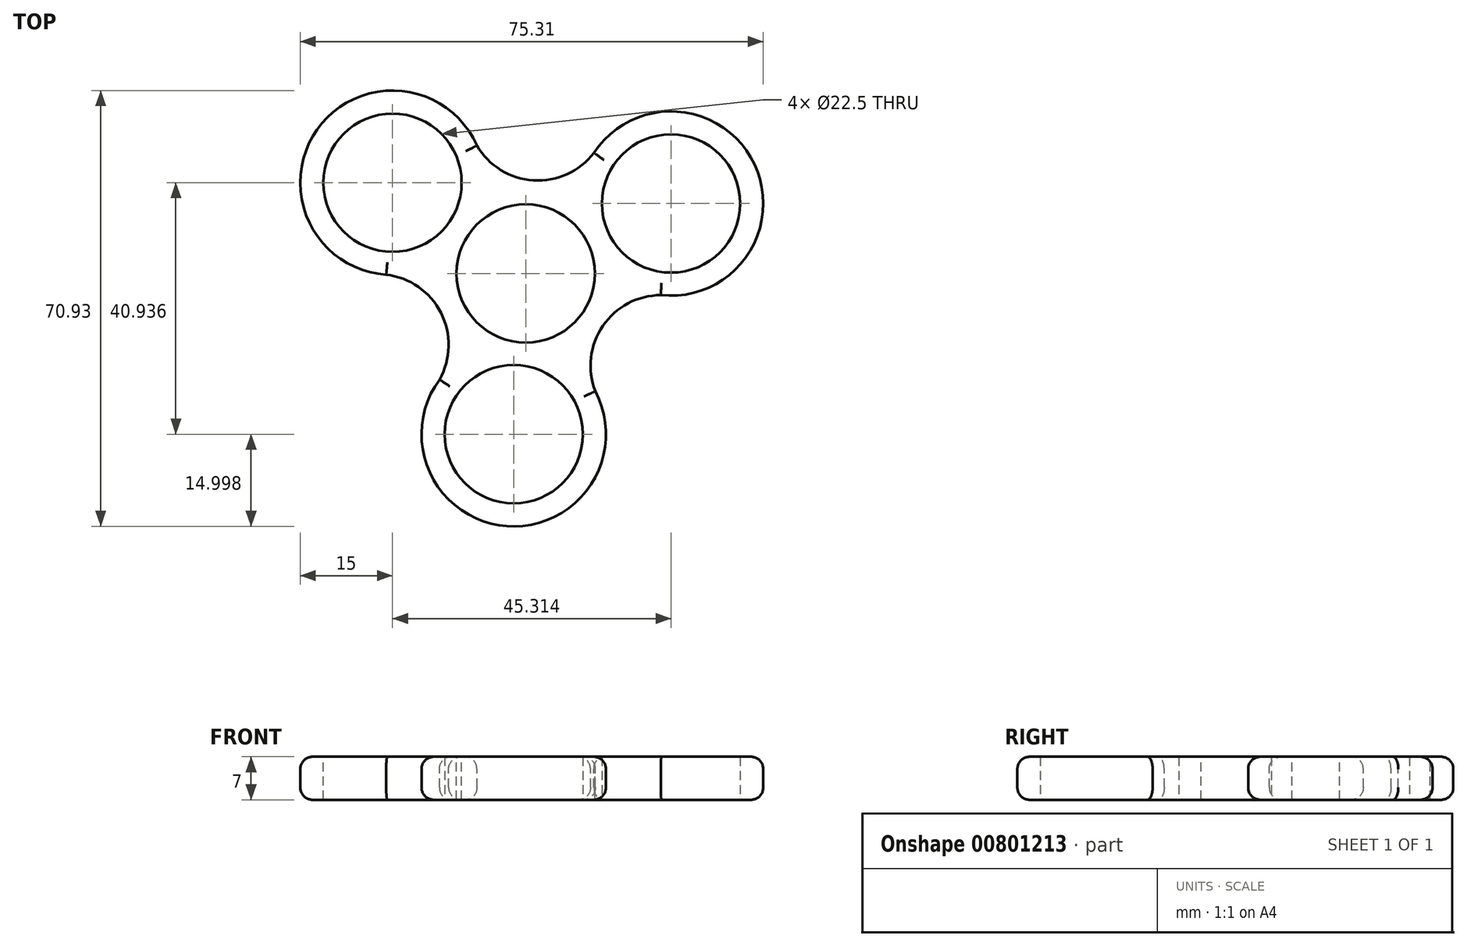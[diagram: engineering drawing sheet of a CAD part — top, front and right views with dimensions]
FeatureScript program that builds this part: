
annotation { "Feature Type Name" : "Feature", "Feature Type Description" : "" }
export const myFeature = defineFeature(function(context is Context, id is Id, definition is map)
    precondition{}
    {
        {
            var Q0;
            Q0=qCreatedBy(makeId("Top.planeOp"),FACE);
            var sketch = newSketch(context, id + "F0", { "sketchPlane" : qUnion([Q0])});
            skCircle(sketch, "E0", {"center": v(0, 0) * mm, "radius": 15 * mm});
            skSolve(sketch);
        }
        {
            var Q0;
            Q0=makeQuery(id+"F0.imprint","IMPRINT",FACE,{"disambiguationData":[TD([[makeQuery(id+"F0.imprint","IMPRINT",EDGE,{"derivedFrom":sQuery(id+"F0.wireOp",EDGE,"E0")}),1.0]])]});
            extrude(context, id + "F1", {"entities" : qUnion([Q0]), "depth" : 7 * mm, "offsetDistance" : 25 * mm});
        }
        {
            var Q0;
            Q0=makeQuery(id+"F1.opExtrude","CAP_EDGE",EDGE,{"disambiguationData":[OSD([sQuery(id+"F0.wireOp",EDGE,"E0")])],"isStart":true});
            fillet(context, id + "F2", {"entities" : qUnion([Q0]), "radius" : 2 * mm, "tangentPropagation" : true, "allowEdgeOverflow" : false});
        }
        {
            var Q0;
            Q0=makeQuery(id+"F1.opExtrude","CAP_EDGE",EDGE,{"disambiguationData":[OSD([sQuery(id+"F0.wireOp",EDGE,"E0")])],"isStart":false});
            fillet(context, id + "F3", {"entities" : qUnion([Q0]), "radius" : 2 * mm, "tangentPropagation" : true, "allowEdgeOverflow" : false});
        }
        {
            var Q0;
            Q0=makeQuery(id+"F1.opExtrude","CAP_FACE",FACE,{"disambiguationData":[OSD([sQuery(id+"F0.wireOp",EDGE,"E0")])],"isStart":false});
            var sketch = newSketch(context, id + "F4", { "sketchPlane" : qUnion([Q0])});
            skCircle(sketch, "E1", {"center": v(0, 0) * mm, "radius": 11.25 * mm});
            skSolve(sketch);
        }
        {
            var Q0;
            Q0 = qSketchRegion(id + "F4", true);
            extrude(context, id + "F5", {"entities" : qUnion([Q0]), "operationType" : NewBodyOperationType.REMOVE, "oppositeDirection" : true, "depth" : 7 * mm, "offsetDistance" : 25 * mm});
        }
        {
            var Q0;
            Q0=makeQuery(id+"F1.opExtrude","CAP_FACE",FACE,{"disambiguationData":[OSD([sQuery(id+"F0.wireOp",EDGE,"E0")])],"isStart":true});
            var sketch = newSketch(context, id + "F6", { "sketchPlane" : qUnion([Q0])});
            skArc(sketch, "E2", {"start": v(3.97, 12.38) * mm, "mid": v(-3.07, 41.12) * mm, "end": v(-5.76, 11.65) * mm});
            skArc(sketch, "E3", {"start": v(3.97, 12.38) * mm, "mid": v(-0.97, 12.96) * mm, "end": v(-5.76, 11.65) * mm});
            skSolve(sketch);
        }
        {
            var Q0;
            {var subQ0=sQuery(id+"F6.wireOp",EDGE,"E2");Q0=makeQuery(id+"F6.imprint","IMPRINT",FACE,{"disambiguationData":[TD([[makeQuery(id+"F6.imprint","IMPRINT",EDGE,{"derivedFrom":subQ0}),1.0]])]});}
            extrude(context, id + "F7", {"entities" : qUnion([Q0]), "operationType" : NewBodyOperationType.ADD, "oppositeDirection" : true, "depth" : 7 * mm, "offsetDistance" : 25 * mm});
        }
        {
            var Q0;
            {var subQ0=sQuery(id+"F0.wireOp",EDGE,"E0");Q0=makeQuery(id+"F7.boolean.opBoolean","MERGE",FACE,{"derivedFrom":[makeQuery(id+"F1.opExtrude","CAP_FACE",FACE,{"disambiguationData":[OSD([subQ0])],"isStart":true}),makeQuery(id+"F7.opExtrude","CAP_FACE",FACE,{"disambiguationData":[OSD([subQ0,sQuery(id+"F6.wireOp",EDGE,"E2")])],"isStart":true})]});}
            var sketch = newSketch(context, id + "F8", { "sketchPlane" : qUnion([Q0])});
            skCircle(sketch, "E4", {"center": v(-1.95, 26.16) * mm, "radius": 11.25 * mm});
            skSolve(sketch);
        }
        {
            var Q0;
            Q0=makeQuery(id+"F8.imprint","IMPRINT",FACE,{"disambiguationData":[TD([[makeQuery(id+"F8.imprint","IMPRINT",EDGE,{"derivedFrom":sQuery(id+"F8.wireOp",EDGE,"E4")}),1.0]])]});
            extrude(context, id + "F9", {"entities" : qUnion([Q0]), "operationType" : NewBodyOperationType.REMOVE, "oppositeDirection" : true, "depth" : 7 * mm, "offsetDistance" : 25 * mm});
        }
        {
            var Q0;
            {var subQ0=sQuery(id+"F0.wireOp",EDGE,"E0");Q0=makeQuery(id+"F7.boolean.opBoolean","MERGE",FACE,{"derivedFrom":[makeQuery(id+"F1.opExtrude","CAP_FACE",FACE,{"disambiguationData":[OSD([subQ0])],"isStart":true}),makeQuery(id+"F7.opExtrude","CAP_FACE",FACE,{"disambiguationData":[OSD([subQ0,sQuery(id+"F6.wireOp",EDGE,"E2")])],"isStart":true})]});}
            var sketch = newSketch(context, id + "F10", { "sketchPlane" : qUnion([Q0])});
            skArc(sketch, "E5", {"start": v(8.74, -9.62) * mm, "mid": v(37.15, -17.9) * mm, "end": v(12.97, -0.84) * mm});
            skArc(sketch, "E6", {"start": v(12.97, -0.84) * mm, "mid": v(10.74, 7.32) * mm, "end": v(3.97, 12.38) * mm});
            skArc(sketch, "E7", {"start": v(8.74, -9.62) * mm, "mid": v(11.71, -5.64) * mm, "end": v(12.97, -0.84) * mm});
            skSolve(sketch);
        }
        {
            var Q0;
            {var subQ0=sQuery(id+"F10.wireOp",EDGE,"E5");Q0=makeQuery(id+"F10.imprint","IMPRINT",FACE,{"disambiguationData":[TD([[makeQuery(id+"F10.imprint","IMPRINT",EDGE,{"derivedFrom":subQ0}),1.0]])]});}
            extrude(context, id + "F11", {"entities" : qUnion([Q0]), "operationType" : NewBodyOperationType.ADD, "oppositeDirection" : true, "depth" : 7 * mm, "offsetDistance" : 25 * mm});
        }
        {
            var Q0;
            {var subQ0=sQuery(id+"F0.wireOp",EDGE,"E0");Q0=makeQuery(id+"F11.boolean.opBoolean","MERGE",FACE,{"derivedFrom":[makeQuery(id+"F7.boolean.opBoolean","MERGE",FACE,{"derivedFrom":[makeQuery(id+"F1.opExtrude","CAP_FACE",FACE,{"disambiguationData":[OSD([subQ0])],"isStart":true}),makeQuery(id+"F7.opExtrude","CAP_FACE",FACE,{"disambiguationData":[OSD([subQ0,sQuery(id+"F6.wireOp",EDGE,"E2")])],"isStart":true})]}),makeQuery(id+"F11.opExtrude","CAP_FACE",FACE,{"disambiguationData":[OSD([subQ0,sQuery(id+"F10.wireOp",EDGE,"E5")])],"isStart":true})]});}
            var sketch = newSketch(context, id + "F12", { "sketchPlane" : qUnion([Q0])});
            skCircle(sketch, "E8", {"center": v(23.63, -11.39) * mm, "radius": 11.25 * mm});
            skSolve(sketch);
        }
        {
            var Q0;
            Q0=makeQuery(id+"F12.imprint","IMPRINT",FACE,{"disambiguationData":[TD([[makeQuery(id+"F12.imprint","IMPRINT",EDGE,{"derivedFrom":sQuery(id+"F12.wireOp",EDGE,"E8")}),1.0]])]});
            extrude(context, id + "F13", {"entities" : qUnion([Q0]), "operationType" : NewBodyOperationType.REMOVE, "oppositeDirection" : true, "depth" : 7 * mm, "offsetDistance" : 25 * mm});
        }
        {
            var Q0;
            {var subQ0=sQuery(id+"F0.wireOp",EDGE,"E0");Q0=makeQuery(id+"F11.boolean.opBoolean","MERGE",FACE,{"derivedFrom":[makeQuery(id+"F7.boolean.opBoolean","MERGE",FACE,{"derivedFrom":[makeQuery(id+"F1.opExtrude","CAP_FACE",FACE,{"disambiguationData":[OSD([subQ0])],"isStart":false}),makeQuery(id+"F7.opExtrude","CAP_FACE",FACE,{"disambiguationData":[OSD([subQ0,sQuery(id+"F6.wireOp",EDGE,"E2")])],"isStart":false})]}),makeQuery(id+"F11.opExtrude","CAP_FACE",FACE,{"disambiguationData":[OSD([subQ0,sQuery(id+"F10.wireOp",EDGE,"E5")])],"isStart":false})]});}
            var sketch = newSketch(context, id + "F14", { "sketchPlane" : qUnion([Q0])});
            skArc(sketch, "E9", {"start": v(-7.21, 10.82) * mm, "mid": v(-34.08, 23.22) * mm, "end": v(-12.7, 2.76) * mm});
            skArc(sketch, "E10", {"start": v(8.74, 9.62) * mm, "mid": v(0.97, 12.96) * mm, "end": v(-7.21, 10.82) * mm});
            skArc(sketch, "E11", {"start": v(-12.7, 2.76) * mm, "mid": v(-11.71, -5.64) * mm, "end": v(-5.76, -11.65) * mm});
            skArc(sketch, "E12", {"start": v(-7.21, 10.82) * mm, "mid": v(-10.74, 7.32) * mm, "end": v(-12.7, 2.76) * mm});
            skSolve(sketch);
        }
        {
            var Q0;
            {var subQ0=sQuery(id+"F14.wireOp",EDGE,"E9");Q0=makeQuery(id+"F14.imprint","IMPRINT",FACE,{"disambiguationData":[TD([[makeQuery(id+"F14.imprint","IMPRINT",EDGE,{"derivedFrom":subQ0}),1.0]])]});}
            extrude(context, id + "F15", {"entities" : qUnion([Q0]), "operationType" : NewBodyOperationType.ADD, "oppositeDirection" : true, "depth" : 7 * mm, "offsetDistance" : 25 * mm});
        }
        {
            var Q0;
            {var subQ0=sQuery(id+"F0.wireOp",EDGE,"E0");Q0=makeQuery(id+"F15.boolean.opBoolean","MERGE",FACE,{"derivedFrom":[makeQuery(id+"F11.boolean.opBoolean","MERGE",FACE,{"derivedFrom":[makeQuery(id+"F7.boolean.opBoolean","MERGE",FACE,{"derivedFrom":[makeQuery(id+"F1.opExtrude","CAP_FACE",FACE,{"disambiguationData":[OSD([subQ0])],"isStart":false}),makeQuery(id+"F7.opExtrude","CAP_FACE",FACE,{"disambiguationData":[OSD([subQ0,sQuery(id+"F6.wireOp",EDGE,"E2")])],"isStart":false})]}),makeQuery(id+"F11.opExtrude","CAP_FACE",FACE,{"disambiguationData":[OSD([subQ0,sQuery(id+"F10.wireOp",EDGE,"E5")])],"isStart":false})]}),makeQuery(id+"F15.opExtrude","CAP_FACE",FACE,{"disambiguationData":[OSD([subQ0,sQuery(id+"F14.wireOp",EDGE,"E9")])],"isStart":true})]});}
            var sketch = newSketch(context, id + "F16", { "sketchPlane" : qUnion([Q0])});
            skCircle(sketch, "E13", {"center": v(-21.68, 14.77) * mm, "radius": 11.25 * mm});
            skSolve(sketch);
        }
        {
            var Q0;
            Q0=makeQuery(id+"F16.imprint","IMPRINT",FACE,{"disambiguationData":[TD([[makeQuery(id+"F16.imprint","IMPRINT",EDGE,{"derivedFrom":sQuery(id+"F16.wireOp",EDGE,"E13")}),1.0]])]});
            extrude(context, id + "F17", {"entities" : qUnion([Q0]), "operationType" : NewBodyOperationType.REMOVE, "oppositeDirection" : true, "depth" : 7 * mm, "offsetDistance" : 25 * mm});
        }
        {
            var Q0;
            Q0=makeQuery(id+"F15.boolean.opBoolean","MERGE",FACE,{"derivedFrom":[makeQuery(id+"F11.boolean.opBoolean","MERGE",FACE,{"derivedFrom":[makeQuery(id+"F7.boolean.opBoolean","MERGE",FACE,{"derivedFrom":[makeQuery(id+"F1.opExtrude","CAP_FACE",FACE,{"disambiguationData":[OSD([sQuery(id+"F0.wireOp",EDGE,"E0")])],"isStart":false}),makeQuery(id+"F7.opExtrude","CAP_FACE",FACE,{"disambiguationData":[OSD([sQuery(id+"F6.wireOp",EDGE,"E2"),sQuery(id+"F6.wireOp",EDGE,"E3")])],"isStart":false})]}),makeQuery(id+"F11.opExtrude","CAP_FACE",FACE,{"disambiguationData":[OSD([sQuery(id+"F10.wireOp",EDGE,"E5"),sQuery(id+"F10.wireOp",EDGE,"E7")])],"isStart":false})]}),makeQuery(id+"F15.opExtrude","CAP_FACE",FACE,{"disambiguationData":[OSD([sQuery(id+"F14.wireOp",EDGE,"E9"),sQuery(id+"F14.wireOp",EDGE,"E12")])],"isStart":true})]});
            var sketch = newSketch(context, id + "F18", { "sketchPlane" : qUnion([Q0])});
            skPoint(sketch, "E14.centerSnap0", {"position": v(0.97, 12.96) * mm});
            skArc(sketch, "E15", {"start": v(-7.95, 20.82) * mm, "mid": v(1.26, 15.15) * mm, "end": v(11.1, 19.62) * mm});
            skSolve(sketch);
        }
        {
            var Q0;
            {var subQ0=sQuery(id+"F18.wireOp",EDGE,"E15");Q0=makeQuery(id+"F18.imprint","IMPRINT",FACE,{"disambiguationData":[TD([[makeQuery(id+"F18.imprint","IMPRINT",EDGE,{"derivedFrom":subQ0}),-1.0]])]});}
            extrude(context, id + "F19", {"entities" : qUnion([Q0]), "operationType" : NewBodyOperationType.ADD, "oppositeDirection" : true, "depth" : 7 * mm, "offsetDistance" : 25 * mm});
        }
        {
            var Q0;
            {var subQ0=sQuery(id+"F14.wireOp",EDGE,"E9");var subQ1=sQuery(id+"F10.wireOp",EDGE,"E5");var subQ2=sQuery(id+"F0.wireOp",EDGE,"E0");Q0=makeQuery(id+"F19.boolean.opBoolean","MERGE",FACE,{"derivedFrom":[makeQuery(id+"F15.boolean.opBoolean","MERGE",FACE,{"derivedFrom":[makeQuery(id+"F11.boolean.opBoolean","MERGE",FACE,{"derivedFrom":[makeQuery(id+"F7.boolean.opBoolean","MERGE",FACE,{"derivedFrom":[makeQuery(id+"F1.opExtrude","CAP_FACE",FACE,{"disambiguationData":[OSD([subQ2])],"isStart":false}),makeQuery(id+"F7.opExtrude","CAP_FACE",FACE,{"disambiguationData":[OSD([sQuery(id+"F6.wireOp",EDGE,"E2"),sQuery(id+"F6.wireOp",EDGE,"E3")])],"isStart":false})]}),makeQuery(id+"F11.opExtrude","CAP_FACE",FACE,{"disambiguationData":[OSD([subQ1,sQuery(id+"F10.wireOp",EDGE,"E7")])],"isStart":false})]}),makeQuery(id+"F15.opExtrude","CAP_FACE",FACE,{"disambiguationData":[OSD([subQ0,sQuery(id+"F14.wireOp",EDGE,"E12")])],"isStart":true})]}),makeQuery(id+"F19.opExtrude","CAP_FACE",FACE,{"disambiguationData":[OSD([subQ2,subQ1,subQ0,sQuery(id+"F18.wireOp",EDGE,"E15")])],"isStart":true})]});}
            var sketch = newSketch(context, id + "F20", { "sketchPlane" : qUnion([Q0])});
            skArc(sketch, "E16", {"start": v(21.97, -3.52) * mm, "mid": v(12.54, -8.54) * mm, "end": v(11.31, -19.16) * mm});
            skSolve(sketch);
        }
        {
            var Q0;
            {var subQ0=sQuery(id+"F20.wireOp",EDGE,"E16");Q0=makeQuery(id+"F20.imprint","IMPRINT",FACE,{"disambiguationData":[TD([[makeQuery(id+"F20.imprint","IMPRINT",EDGE,{"derivedFrom":subQ0}),-1.0]])]});}
            extrude(context, id + "F21", {"entities" : qUnion([Q0]), "operationType" : NewBodyOperationType.ADD, "oppositeDirection" : true, "depth" : 7 * mm, "offsetDistance" : 25 * mm});
        }
        {
            var Q0;
            {var subQ0=sQuery(id+"F10.wireOp",EDGE,"E5");var subQ1=sQuery(id+"F6.wireOp",EDGE,"E2");var subQ2=sQuery(id+"F0.wireOp",EDGE,"E0");var subQ3=sQuery(id+"F14.wireOp",EDGE,"E9");Q0=makeQuery(id+"F21.boolean.opBoolean","MERGE",FACE,{"derivedFrom":[makeQuery(id+"F19.boolean.opBoolean","MERGE",FACE,{"derivedFrom":[makeQuery(id+"F15.boolean.opBoolean","MERGE",FACE,{"derivedFrom":[makeQuery(id+"F11.boolean.opBoolean","MERGE",FACE,{"derivedFrom":[makeQuery(id+"F7.boolean.opBoolean","MERGE",FACE,{"derivedFrom":[makeQuery(id+"F1.opExtrude","CAP_FACE",FACE,{"disambiguationData":[OSD([subQ2])],"isStart":false}),makeQuery(id+"F7.opExtrude","CAP_FACE",FACE,{"disambiguationData":[OSD([subQ1,sQuery(id+"F6.wireOp",EDGE,"E3")])],"isStart":false})]}),makeQuery(id+"F11.opExtrude","CAP_FACE",FACE,{"disambiguationData":[OSD([subQ0,sQuery(id+"F10.wireOp",EDGE,"E7")])],"isStart":false})]}),makeQuery(id+"F15.opExtrude","CAP_FACE",FACE,{"disambiguationData":[OSD([subQ3,sQuery(id+"F14.wireOp",EDGE,"E12")])],"isStart":true})]}),makeQuery(id+"F19.opExtrude","CAP_FACE",FACE,{"disambiguationData":[OSD([subQ2,subQ0,subQ3,sQuery(id+"F18.wireOp",EDGE,"E15")])],"isStart":true})]}),makeQuery(id+"F21.opExtrude","CAP_FACE",FACE,{"disambiguationData":[OSD([subQ2,subQ1,subQ0,sQuery(id+"F20.wireOp",EDGE,"E16")])],"isStart":true})]});}
            var sketch = newSketch(context, id + "F22", { "sketchPlane" : qUnion([Q0])});
            skArc(sketch, "E17", {"start": v(-14.04, -17.27) * mm, "mid": v(-13.8, -6.4) * mm, "end": v(-22.7, -0.2) * mm});
            skSolve(sketch);
        }
        {
            var Q0;
            {var subQ0=sQuery(id+"F22.wireOp",EDGE,"E17");Q0=makeQuery(id+"F22.imprint","IMPRINT",FACE,{"disambiguationData":[TD([[makeQuery(id+"F22.imprint","IMPRINT",EDGE,{"derivedFrom":subQ0}),-1.0]])]});}
            extrude(context, id + "F23", {"entities" : qUnion([Q0]), "operationType" : NewBodyOperationType.ADD, "oppositeDirection" : true, "depth" : 7 * mm, "offsetDistance" : 25 * mm});
        }
        {
            var Q0;
            Q0=makeQuery(id+"F23.opExtrude","CAP_EDGE",EDGE,{"disambiguationData":[OSD([sQuery(id+"F22.wireOp",EDGE,"E17")])],"isStart":true});
            var Q1;
            Q1=makeQuery(id+"F7.opExtrude","CAP_EDGE",EDGE,{"disambiguationData":[OSD([sQuery(id+"F6.wireOp",EDGE,"E2")])],"isStart":false});
            var Q2;
            Q2=makeQuery(id+"F21.opExtrude","CAP_EDGE",EDGE,{"disambiguationData":[OSD([sQuery(id+"F20.wireOp",EDGE,"E16")])],"isStart":true});
            var Q3;
            Q3=makeQuery(id+"F11.opExtrude","CAP_EDGE",EDGE,{"disambiguationData":[OSD([sQuery(id+"F10.wireOp",EDGE,"E5")])],"isStart":false});
            var Q4;
            Q4=makeQuery(id+"F19.opExtrude","CAP_EDGE",EDGE,{"disambiguationData":[OSD([sQuery(id+"F18.wireOp",EDGE,"E15")])],"isStart":true});
            var Q5;
            Q5=makeQuery(id+"F15.opExtrude","CAP_EDGE",EDGE,{"disambiguationData":[OSD([sQuery(id+"F14.wireOp",EDGE,"E9")])],"isStart":true});
            fillet(context, id + "F24", {"entities" : qUnion([Q0, Q1, Q2, Q3, Q4, Q5]), "radius" : 2 * mm, "tangentPropagation" : true, "allowEdgeOverflow" : false});
        }
        {
            var Q0;
            Q0=makeQuery(id+"F21.opExtrude","CAP_EDGE",EDGE,{"disambiguationData":[OSD([sQuery(id+"F20.wireOp",EDGE,"E16")])],"isStart":false});
            var Q1;
            Q1=makeQuery(id+"F11.opExtrude","CAP_EDGE",EDGE,{"disambiguationData":[OSD([sQuery(id+"F10.wireOp",EDGE,"E5")])],"isStart":true});
            var Q2;
            Q2=makeQuery(id+"F19.opExtrude","CAP_EDGE",EDGE,{"disambiguationData":[OSD([sQuery(id+"F18.wireOp",EDGE,"E15")])],"isStart":false});
            var Q3;
            Q3=makeQuery(id+"F15.opExtrude","CAP_EDGE",EDGE,{"disambiguationData":[OSD([sQuery(id+"F14.wireOp",EDGE,"E9")])],"isStart":false});
            var Q4;
            Q4=makeQuery(id+"F23.opExtrude","CAP_EDGE",EDGE,{"disambiguationData":[OSD([sQuery(id+"F22.wireOp",EDGE,"E17")])],"isStart":false});
            var Q5;
            Q5=makeQuery(id+"F7.opExtrude","CAP_EDGE",EDGE,{"disambiguationData":[OSD([sQuery(id+"F6.wireOp",EDGE,"E2")])],"isStart":true});
            fillet(context, id + "F25", {"entities" : qUnion([Q0, Q1, Q2, Q3, Q4, Q5]), "radius" : 2 * mm, "tangentPropagation" : true, "allowEdgeOverflow" : false});
        }
    });
